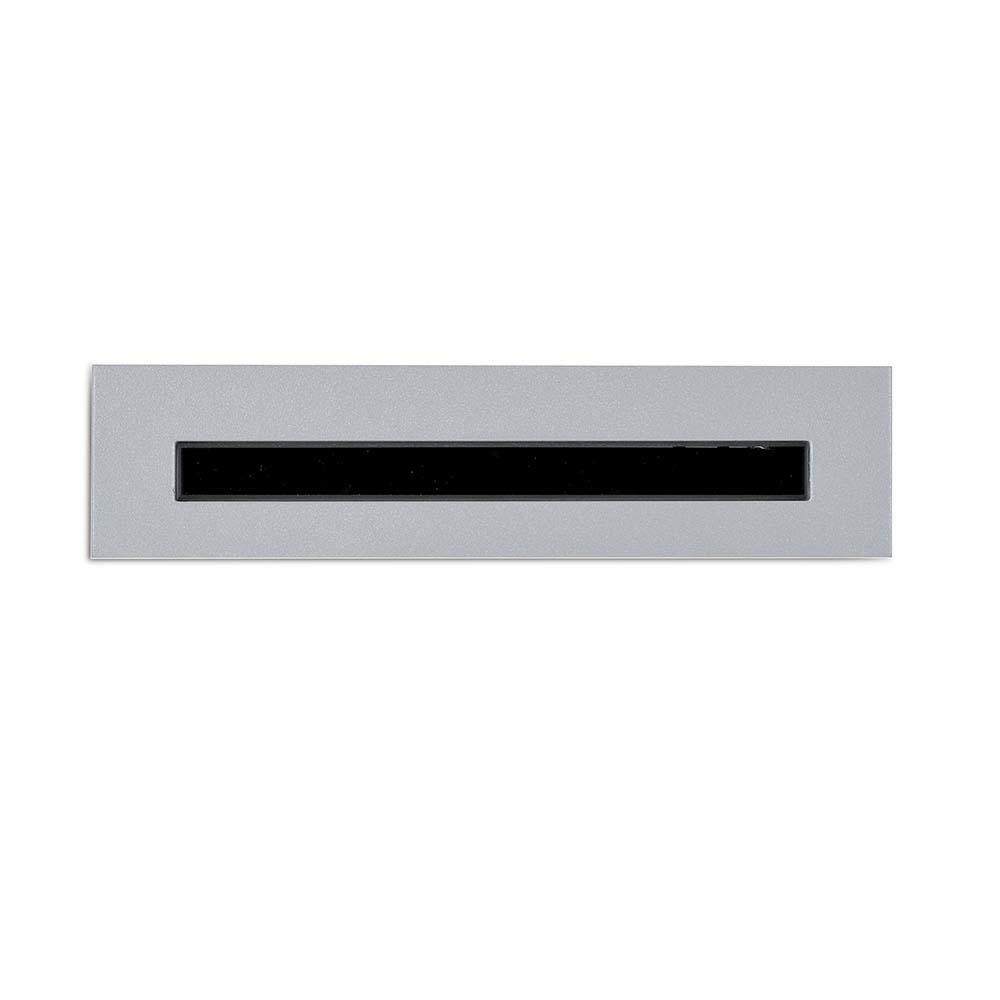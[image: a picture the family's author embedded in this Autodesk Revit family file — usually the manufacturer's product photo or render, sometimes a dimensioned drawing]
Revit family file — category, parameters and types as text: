
# Revit family: Platek_Mask
name_source: partatom
category: Apparecchi per illuminazione
revit_build: Autodesk Revit 2017 (Build: 20160225_1515(x64)
units: mm (PartAtom-declared; Revit-internal decimal feet)

## family parameters
Condiviso = No
Host = Superficie
Punto di calcolo locali = No
Quota connettore circolare = Usa diametro
Sorgente d'illuminazione = Sì
Taglio con vuoti quando caricato = Sì
Tipo di parte = Normale

## types (1)
- 3450601_2,8W_LED_3000K
    Angolo inclinazione = -90.00°
    Body = PLK_06_Grey
    CRI = >80
    Cable Lenght = Cable length 0,2 m(3x1mm2)
    Carico apparente = 0 VA
    Codice assieme = 3450601.06(Grey);3450601.01(Black);3450601.02(White);3455911.07(Corten);3450601.08(Anthracite);3450601.09(Bronze)
    Colour Temperature = 3000 K
    Commenti sul tipo = Paths, Ramps, Steps
    Descrizione = Outdoor Lighting, Wall mounted
    Diffuse Type = flat tempered extra clear glass
    Dimmable = NO
    Emetti da larghezza rettangolo = 1 mm  [stored 0.00328084 ft]
    Emetti da lunghezza rettangolo = 10 mm  [stored 0.0328084 ft]
    Energy Efficiency Rating = A/A+/A++
    File diagramma fotometrico = 3450601.IES
    Filtro dei colori = 16777215
    IK Rating = IK07
    IP Rating = IP65
    Immagine tipo = frame_1_ph_original.jpg
    Insulation Class = 3
    LED Protection = Surge Protection Included
    Lampada = LED
    Light Source = PLK_Light Source
    Luminaire Luminous Flux = 10 lm
    Luminaire Luminous Intensity = 64 cd
    Luminaire Wattage = 3 W
    Manufacturer Comment = 5mm flat tempered glass
    Modello = Mask
    Mounting Type = Wall Recessed
    Nota chiave = Other LED colors available on request
    PLATEK Article Code = 3450601+9920050(Recessed Box)
    Part Body = PLK_Plastic_Black
    Power Supply Unit = Included
    Product Dimension = L50mm x W72 mm x 205mm
    Product Documentation Link = http://www.platek.eu
    Product Page URL = http://www.platek.eu
    Produttore = PLATEK SRL
    Prospetto di default = 1219 mm
    Recessed Box = PLK_Plastic_Black
    Rendi la forma visibile nel rendering = No
    URL = www.platek.eu
    Variazione temperatura colore lampada con luminosità attenuata = <Nessuno>
    Voltage Output = 12 V

note: [stored X ft] marks values corroborated as IEEE doubles in the binary element streams (Revit-internal decimal feet)
